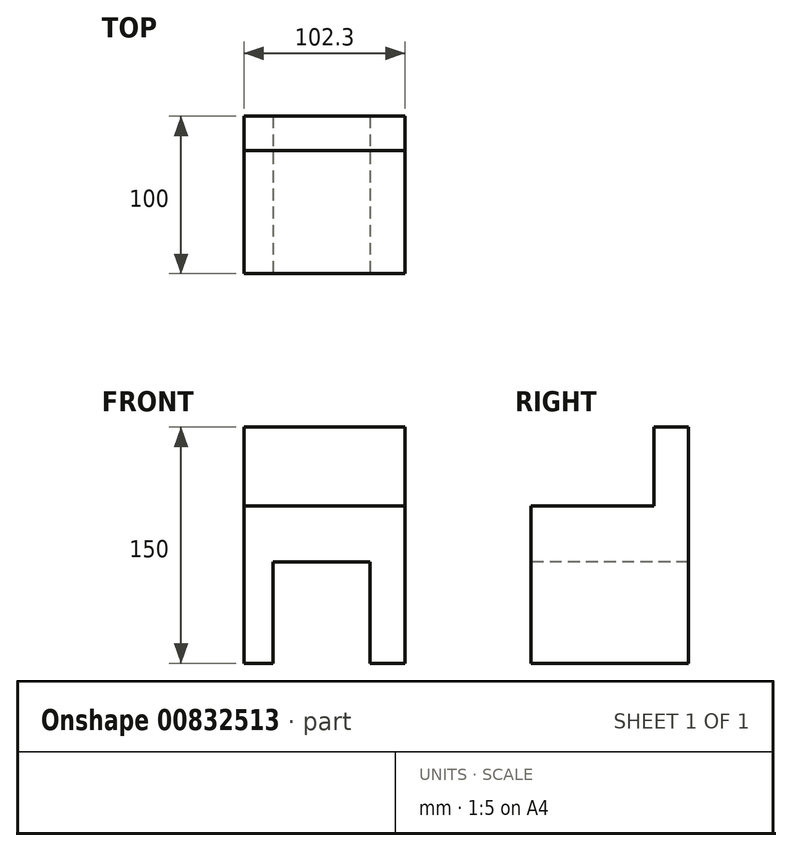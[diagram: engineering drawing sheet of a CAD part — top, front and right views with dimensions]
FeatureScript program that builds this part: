
annotation { "Feature Type Name" : "Feature", "Feature Type Description" : "" }
export const myFeature = defineFeature(function(context is Context, id is Id, definition is map)
    precondition{}
    {
        {
            var Q0;
            Q0=qCreatedBy(makeId("Top.planeOp"),FACE);
            var sketch = newSketch(context, id + "F0", { "sketchPlane" : qUnion([Q0])});
            skLineSegment(sketch, "E0.bottom", {"start": v(-53.41, -44.43) * mm, "end": v(48.89, -44.43) * mm});
            skLineSegment(sketch, "E0.top", {"start": v(-53.41, 55.57) * mm, "end": v(48.89, 55.57) * mm});
            skLineSegment(sketch, "E0.left", {"start": v(-53.41, -44.43) * mm, "end": v(-53.41, 55.57) * mm});
            skLineSegment(sketch, "E0.right", {"start": v(48.89, -44.43) * mm, "end": v(48.89, 55.57) * mm});
            skSolve(sketch);
        }
        {
            var Q0;
            Q0 = qSketchRegion(id + "F0", true);
            extrude(context, id + "F1", {"entities" : qUnion([Q0]), "depth" : 100 * mm, "offsetDistance" : 25 * mm});
        }
        {
            var Q0;
            Q0=makeQuery(id+"F1.opExtrude","CAP_FACE",FACE,{"disambiguationData":[OSD([sQuery(id+"F0.wireOp",EDGE,"E0.bottom"),sQuery(id+"F0.wireOp",EDGE,"E0.top"),sQuery(id+"F0.wireOp",EDGE,"E0.left"),sQuery(id+"F0.wireOp",EDGE,"E0.right")])],"isStart":false});
            var sketch = newSketch(context, id + "F2", { "sketchPlane" : qUnion([Q0])});
            skLineSegment(sketch, "E1.bottom", {"start": v(-53.41, 55.57) * mm, "end": v(48.89, 55.57) * mm});
            skLineSegment(sketch, "E1.top", {"start": v(-53.41, 33.73) * mm, "end": v(48.89, 33.73) * mm});
            skLineSegment(sketch, "E1.left", {"start": v(-53.41, 55.57) * mm, "end": v(-53.41, 33.73) * mm});
            skLineSegment(sketch, "E1.right", {"start": v(48.89, 55.57) * mm, "end": v(48.89, 33.73) * mm});
            skSolve(sketch);
        }
        {
            var Q0;
            Q0 = qSketchRegion(id + "F2", true);
            extrude(context, id + "F3", {"entities" : qUnion([Q0]), "operationType" : NewBodyOperationType.ADD, "depth" : 25 * mm, "offsetDistance" : 25 * mm});
        }
        {
            var Q0;
            Q0=makeQuery(id+"F1.opExtrude","SWEPT_FACE",FACE,{"disambiguationData":[OSD([sQuery(id+"F0.wireOp",EDGE,"E0.bottom")])]});
            var sketch = newSketch(context, id + "F4", { "sketchPlane" : qUnion([Q0])});
            skLineSegment(sketch, "E2.bottom", {"start": v(26.77, 0) * mm, "end": v(-34.81, 0) * mm});
            skLineSegment(sketch, "E2.top", {"start": v(26.77, 64.38) * mm, "end": v(-34.81, 64.38) * mm});
            skLineSegment(sketch, "E2.left", {"start": v(26.77, 0) * mm, "end": v(26.77, 64.38) * mm});
            skLineSegment(sketch, "E2.right", {"start": v(-34.81, 0) * mm, "end": v(-34.81, 64.38) * mm});
            skSolve(sketch);
        }
        {
            var Q0;
            Q0 = qSketchRegion(id + "F4", true);
            extrude(context, id + "F5", {"entities" : qUnion([Q0]), "operationType" : NewBodyOperationType.REMOVE, "endBound" : BoundingType.THROUGH_ALL, "oppositeDirection" : true, "depth" : 25 * mm, "offsetDistance" : 25 * mm});
        }
        {
            var Q0;
            Q0=makeQuery(id+"F3.opExtrude","CAP_FACE",FACE,{"disambiguationData":[OSD([sQuery(id+"F2.wireOp",EDGE,"E1.bottom"),sQuery(id+"F2.wireOp",EDGE,"E1.top"),sQuery(id+"F2.wireOp",EDGE,"E1.left"),sQuery(id+"F2.wireOp",EDGE,"E1.right")])],"isStart":false});
            var sketch = newSketch(context, id + "F6", { "sketchPlane" : qUnion([Q0])});
            skLineSegment(sketch, "E3.bottom", {"start": v(48.89, 33.73) * mm, "end": v(-53.41, 33.73) * mm});
            skLineSegment(sketch, "E3.top", {"start": v(48.89, 55.57) * mm, "end": v(-53.41, 55.57) * mm});
            skLineSegment(sketch, "E3.left", {"start": v(48.89, 33.73) * mm, "end": v(48.89, 55.57) * mm});
            skLineSegment(sketch, "E3.right", {"start": v(-53.41, 33.73) * mm, "end": v(-53.41, 55.57) * mm});
            skSolve(sketch);
        }
        {
            var Q0;
            Q0 = qSketchRegion(id + "F6", true);
            extrude(context, id + "F7", {"entities" : qUnion([Q0]), "operationType" : NewBodyOperationType.ADD, "depth" : 25 * mm, "offsetDistance" : 25 * mm});
        }
    });
